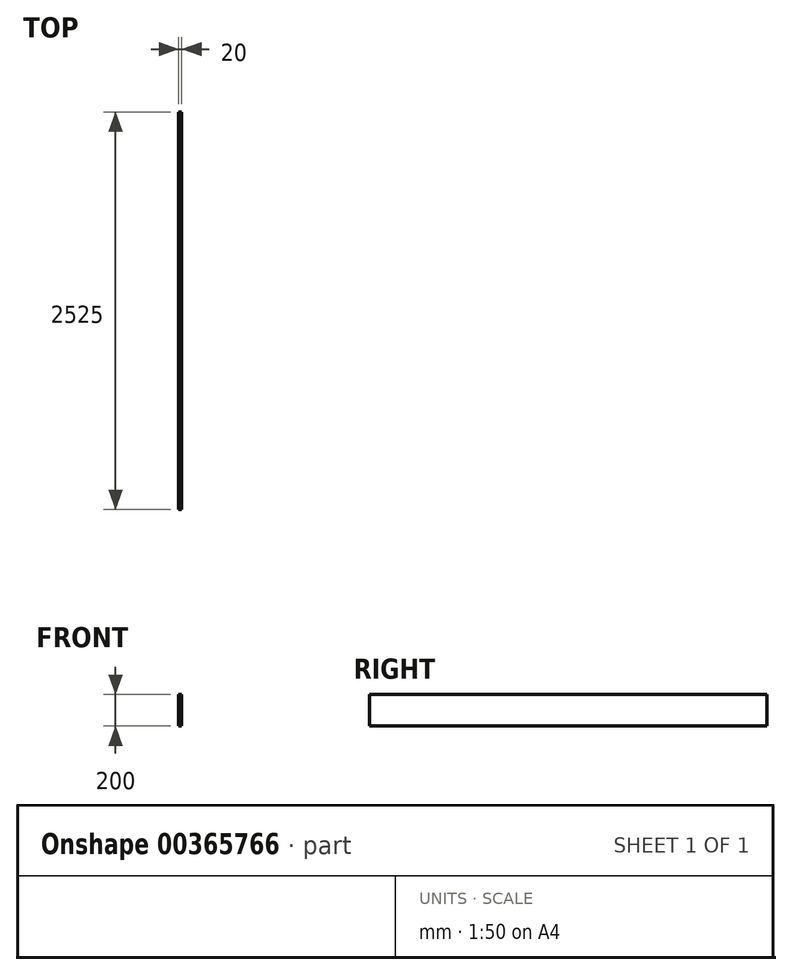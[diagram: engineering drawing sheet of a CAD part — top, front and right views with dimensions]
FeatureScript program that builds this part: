
annotation { "Feature Type Name" : "Feature", "Feature Type Description" : "" }
export const myFeature = defineFeature(function(context is Context, id is Id, definition is map)
    precondition{}
    {
        {
            var Q0;
            Q0=qCreatedBy(makeId("Front.planeOp"),FACE);
            var sketch = newSketch(context, id + "F0", { "sketchPlane" : qUnion([Q0])});
            skLineSegment(sketch, "E0.bottom", {"start": v(-10, 100) * mm, "end": v(10, 100) * mm});
            skLineSegment(sketch, "E0.top", {"start": v(-10, -100) * mm, "end": v(10, -100) * mm});
            skLineSegment(sketch, "E0.left", {"start": v(-10, 100) * mm, "end": v(-10, -100) * mm});
            skLineSegment(sketch, "E0.right", {"start": v(10, 100) * mm, "end": v(10, -100) * mm});
            skPoint(sketch, "E0.middle", {"position": v(0, 0) * mm});
            skSolve(sketch);
        }
        {
            var Q0;
            Q0=makeQuery(id+"F0.imprint","IMPRINT",FACE,{"disambiguationData":[TD([[makeQuery(id+"F0.imprint","IMPRINT",EDGE,{"derivedFrom":sQuery(id+"F0.wireOp",EDGE,"E0.bottom")}),-1.0]])]});
            extrude(context, id + "F1", {"entities" : qUnion([Q0]), "endBound" : BoundingType.SYMMETRIC, "depth" : 2525 * mm});
        }
    });
